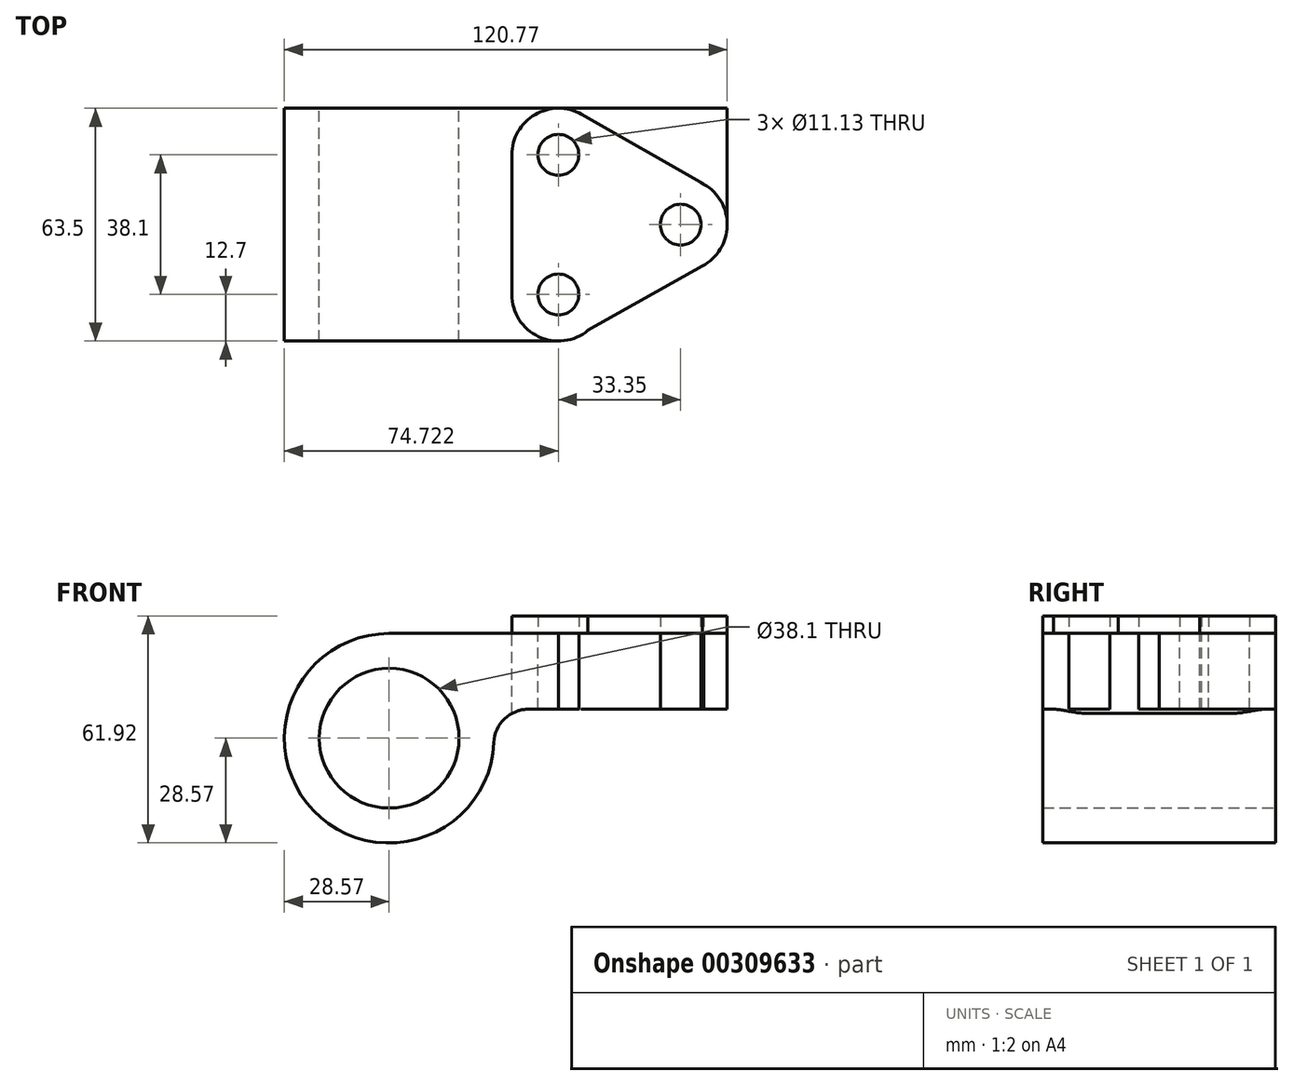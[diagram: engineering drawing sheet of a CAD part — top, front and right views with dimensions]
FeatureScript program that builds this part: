
annotation { "Feature Type Name" : "Feature", "Feature Type Description" : "" }
export const myFeature = defineFeature(function(context is Context, id is Id, definition is map)
    precondition{}
    {
        {
            var Q0;
            Q0=qCreatedBy(makeId("Front.planeOp"),FACE);
            var sketch = newSketch(context, id + "F0", { "sketchPlane" : qUnion([Q0])});
            skCircle(sketch, "E0", {"center": v(0, 0) * mm, "radius": 19.05 * mm});
            skLineSegment(sketch, "E1", {"start": v(0, 41.7) * mm, "end": v(0, -43.76) * mm, "construction": true});
            skArc(sketch, "E2", {"start": v(0, 28.58) * mm, "mid": v(-17.18, -22.84) * mm, "end": v(27.45, 7.92) * mm});
            skLineSegment(sketch, "E3", {"start": v(0, 28.58) * mm, "end": v(50.8, 28.58) * mm});
            skLineSegment(sketch, "E4", {"start": v(50.8, 28.58) * mm, "end": v(79.5, 28.58) * mm});
            skLineSegment(sketch, "E5", {"start": v(79.5, 28.58) * mm, "end": v(92.2, 28.58) * mm});
            skLineSegment(sketch, "E6", {"start": v(92.2, 28.58) * mm, "end": v(92.2, 7.92) * mm});
            skLineSegment(sketch, "E7", {"start": v(92.2, 7.92) * mm, "end": v(27.45, 7.92) * mm});
            skSolve(sketch);
        }
        {
            var Q0;
            Q0=makeQuery(id+"F0.imprint","IMPRINT",FACE,{"disambiguationData":[TD([[makeQuery(id+"F0.imprint","IMPRINT",EDGE,{"derivedFrom":sQuery(id+"F0.wireOp",EDGE,"E0")}),-1.0]])]});
            extrude(context, id + "F1", {"entities" : qUnion([Q0]), "depth" : 63.5 * mm});
        }
        {
            var Q0;
            Q0=makeQuery(id+"F1.opExtrude","SWEPT_EDGE",EDGE,{"disambiguationData":[OSD([sQuery(id+"F0.wireOp",EDGE,"E2"),sQuery(id+"F0.wireOp",EDGE,"E7")])]});
            fillet(context, id + "F2", {"entities" : qUnion([Q0]), "radius" : 9.52 * mm, "tangentPropagation" : true, "allowEdgeOverflow" : false});
        }
        {
            var Q0;
            Q0=makeQuery(id+"F1.opExtrude","SWEPT_FACE",FACE,{"disambiguationData":[OSD([sQuery(id+"F0.wireOp",EDGE,"E3"),sQuery(id+"F0.wireOp",EDGE,"E4"),sQuery(id+"F0.wireOp",EDGE,"E5")])]});
            var sketch = newSketch(context, id + "F3", { "sketchPlane" : qUnion([Q0])});
            skLineSegment(sketch, "E8", {"start": v(92.2, -31.75) * mm, "end": v(79.5, -31.75) * mm, "construction": true});
            skPoint(sketch, "E8.endSnap0", {"position": v(92.2, -31.75) * mm});
            skCircle(sketch, "E9", {"center": v(79.5, -31.75) * mm, "radius": 5.56 * mm});
            skCircle(sketch, "E10", {"center": v(46.15, -50.8) * mm, "radius": 5.56 * mm});
            skCircle(sketch, "E11", {"center": v(46.15, -12.7) * mm, "radius": 5.56 * mm});
            skArc(sketch, "E12", {"start": v(84.9, -20.26) * mm, "mid": v(92.2, -31.49) * mm, "end": v(85.38, -43) * mm});
            skArc(sketch, "E13", {"start": v(46.15, 0) * mm, "mid": v(37.17, -3.72) * mm, "end": v(33.45, -12.7) * mm});
            skArc(sketch, "E14", {"start": v(46.15, -63.5) * mm, "mid": v(37.17, -59.78) * mm, "end": v(33.45, -50.8) * mm});
            skLineSegment(sketch, "E15", {"start": v(33.45, -12.7) * mm, "end": v(33.45, -50.8) * mm});
            skLineSegment(sketch, "E16", {"start": v(85.38, -43) * mm, "end": v(85.85, -42.76) * mm});
            skPoint(sketch, "E16.endSnap0", {"position": v(85.85, -31.75) * mm});
            skLineSegment(sketch, "E17", {"start": v(85.85, -20.75) * mm, "end": v(84.9, -20.26) * mm});
            skArc(sketch, "E18", {"start": v(46.15, -63.5) * mm, "mid": v(50.45, -62.75) * mm, "end": v(54.23, -60.6) * mm});
            skArc(sketch, "E19", {"start": v(46.15, 0) * mm, "mid": v(49.41, -0.43) * mm, "end": v(52.45, -1.67) * mm});
            skLineSegment(sketch, "E20", {"start": v(85.85, -20.75) * mm, "end": v(52.03, -1.43) * mm});
            skPoint(sketch, "E20.endSnap0", {"position": v(52.03, -1.44) * mm});
            skLineSegment(sketch, "E21", {"start": v(85.38, -43) * mm, "end": v(54.23, -60.6) * mm});
            skSolve(sketch);
        }
        {
            var Q0;
            {var subQ7=sQuery(id+"F3.wireOp",EDGE,"E18");Q0=makeQuery(id+"F3.imprint","IMPRINT",FACE,{"disambiguationData":[TD([[makeQuery(id+"F3.imprint","IMPRINT",EDGE,{"derivedFrom":subQ7}),-1.0]])]});}
            var Q1;
            {var subQ0=sQuery(id+"F3.wireOp",EDGE,"E19");Q1=makeQuery(id+"F3.imprint","IMPRINT",FACE,{"disambiguationData":[TD([[makeQuery(id+"F3.imprint","IMPRINT",EDGE,{"derivedFrom":subQ0}),1.0]])]});}
            extrude(context, id + "F4", {"entities" : qUnion([Q0, Q1]), "operationType" : NewBodyOperationType.REMOVE, "endBound" : BoundingType.THROUGH_ALL, "oppositeDirection" : true, "depth" : 25.4 * mm});
        }
        {
            var Q0;
            Q0=makeQuery(id+"F3.imprint","IMPRINT",FACE,{"disambiguationData":[TD([[makeQuery(id+"F3.imprint","IMPRINT",EDGE,{"derivedFrom":sQuery(id+"F3.wireOp",EDGE,"E9")}),-1.0]])]});
            extrude(context, id + "F5", {"entities" : qUnion([Q0]), "operationType" : NewBodyOperationType.ADD, "depth" : 4.78 * mm});
        }
    });
